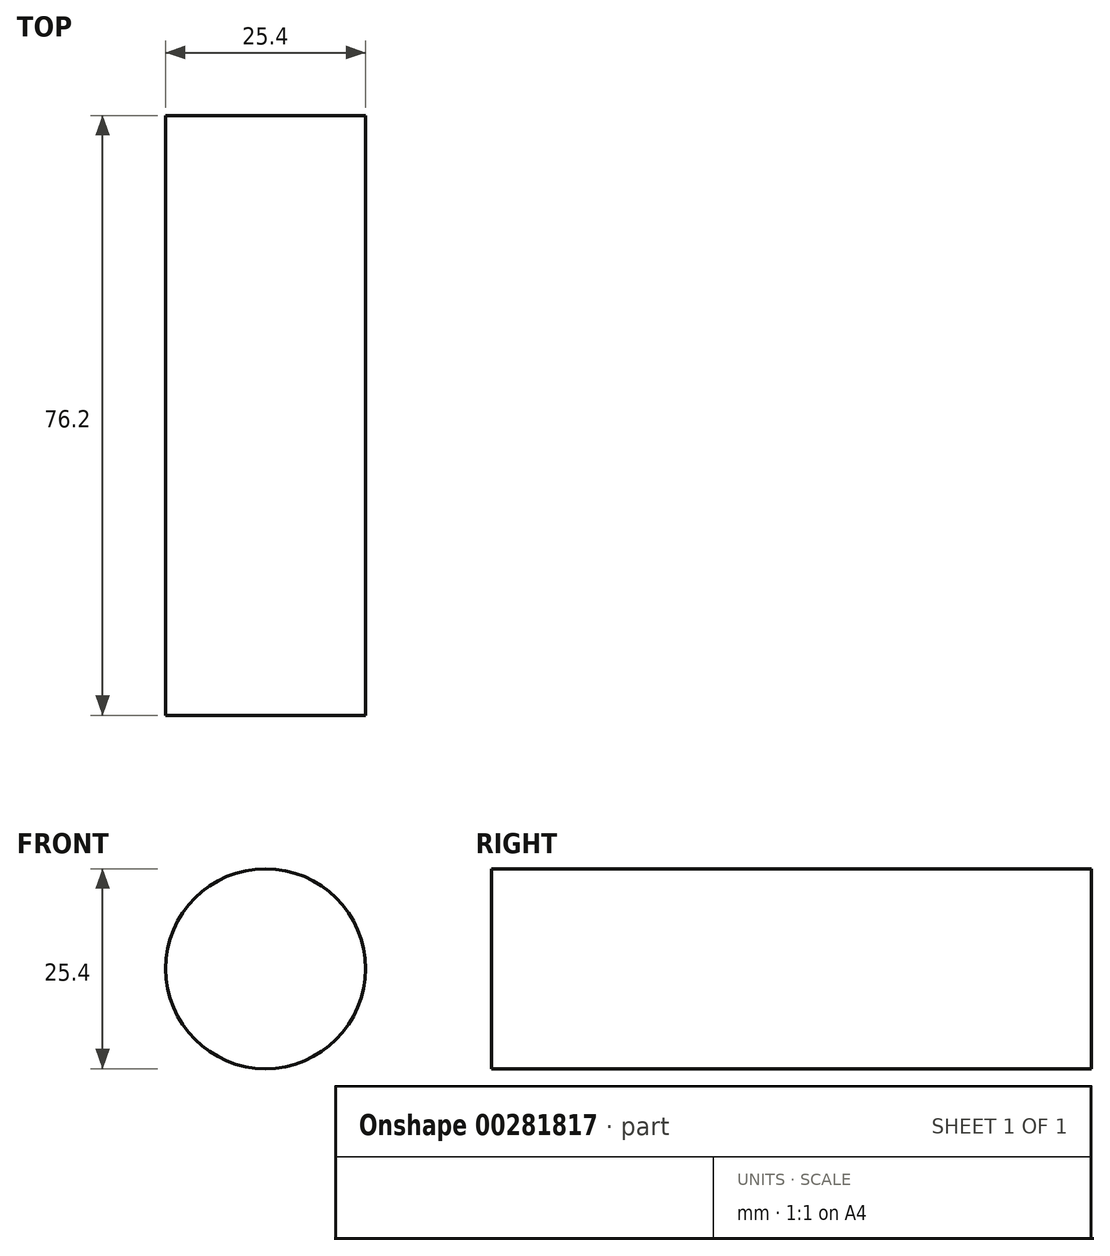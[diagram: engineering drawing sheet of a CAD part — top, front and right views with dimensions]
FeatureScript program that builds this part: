
annotation { "Feature Type Name" : "Feature", "Feature Type Description" : "" }
export const myFeature = defineFeature(function(context is Context, id is Id, definition is map)
    precondition{}
    {
        {
            var Q0;
            Q0=qCreatedBy(makeId("Front.planeOp"),FACE);
            var sketch = newSketch(context, id + "F0", { "sketchPlane" : qUnion([Q0])});
            skCircle(sketch, "E0", {"center": v(-27.13, 35.18) * mm, "radius": 12.7 * mm});
            skSolve(sketch);
        }
        {
            var Q0;
            Q0 = qSketchRegion(id + "F0", true);
            extrude(context, id + "F1", {"entities" : qUnion([Q0]), "depth" : 76.2 * mm});
        }
    });
